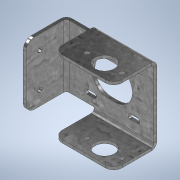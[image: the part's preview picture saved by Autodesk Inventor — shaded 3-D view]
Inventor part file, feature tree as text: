
AUTODESK INVENTOR PART (.ipt)
format: ipt  version: 2022 (Build 260153000, 153)  size: 364,544 bytes
history: native  units: in
note: dims shown in document units (in); Inventor stores cm internally (conversion verified against a paired STEP export)
features: sheet_metal_op x7, other x5, sketch x4, hole x2, chamfer x1
ambient origin geometry x8: Origin, YZ Plane, XZ Plane, XY Plane, X Axis, Y Axis, Z Axis, Center Point
bodies: Solid2 (feature_tree)
feature tree (19):
  sheet_metal_op  "Face1"
  sheet_metal_op  "Flange2"
  sketch  "Sketch3"  dims[d1=2.1654in d4=1.2205in]
  hole  "Hole2"  [1 undecoded]
  sheet_metal_op  "Flange3"
  chamfer  "Corner Round2"
  hole  "Hole3"  [1 undecoded]
  other  "Plate1"
  sketch  "Sketch6"  dims[d7=1.2205in d8=1.2205in]
  other  "Plate4"
  sheet_metal_op  "Bend3"
  sheet_metal_op  "Corner2"
  sketch  "Sketch7"  dims[d9=1.2205in]
  other  "Plate5"
  sheet_metal_op  "Bend4"
  sheet_metal_op  "Corner3"
  sketch  "Sketch8"  dims[d10=1.2205in d11=0.0669in d12=0.1969in d13=0.4724in d14=0.1969in d15=0.5906in d16=0.08in d36=0.5512in d41=0.08in d42=0.0in d43=0.1339in d44=0.2362in d45=0.2559in d46=0.1181in d47=90.0deg d48=0.315in d49=0.8108in d53=2.4803in d55=0.4921in d56=0.4921in d83=1.6929in d84=0.1969in d85=0.5512in d86=0.08in d87=0.04in d88=0.16in d89=0.08in d90=1.2205in d91=90.0deg d92=0.08in d93=0.32in d94=0.08in d95=0.08in d96=0.3937in d97=0.1575in d98=0.2362in d99=0.08in d100=0.04in d101=0.16in d102=0.08in d103=1.2205in d104=90.0deg d105=0.08in d106=0.32in d107=0.08in d108=0.08in d109=0.3937in d110=0.3937in d111=0.3937in d112=0.1339in d113=0.2362in d114=0.2559in d115=0.1181in d116=0.6181in d117=0.08in d118=0.8108in]
  other  "Cut1"
  other  "Definition1"
note: 2 required parameter values undecoded (feature->parameter linkage not recoverable at this tier; creation-order binding heuristic only, values carry confidence <= 0.55)
